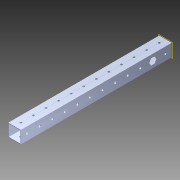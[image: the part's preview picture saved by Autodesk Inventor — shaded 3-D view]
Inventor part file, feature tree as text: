
AUTODESK INVENTOR PART (.ipt)
format: ipt  version: 2014 SP1 (Build 180222100, 222)  size: 1,234,944 bytes
history: native  units: in
note: dims shown in document units (in); Inventor stores cm internally (conversion verified against a paired STEP export)
features: extrude x2, sketch x2, pattern_circular x1, other x1, plane x1, imported_body x1
ambient origin geometry x8: Origin, YZ Plane, XZ Plane, XY Plane, X Axis, Y Axis, Z Axis, Center Point
bodies: Body1 (feature_tree)
feature tree (8):
  pattern_circular  "CirPattern2"
  other  "217-3426-STEP1"
  plane  "Work Plane1"
  extrude  "Extrusion1"  Depth=3937.0079in TaperAngle=0.0deg
  extrude  "Extrusion2"  Depth=0.5in TaperAngle=0.0deg
  imported_body  "Base1"
  sketch  "Sketch1"  dims[d0=-12.0in d1=3937.0079in d2=0.0in]
  sketch  "Sketch3"  dims[d3=0.5in d4=39.3701in d5=0.0in]
